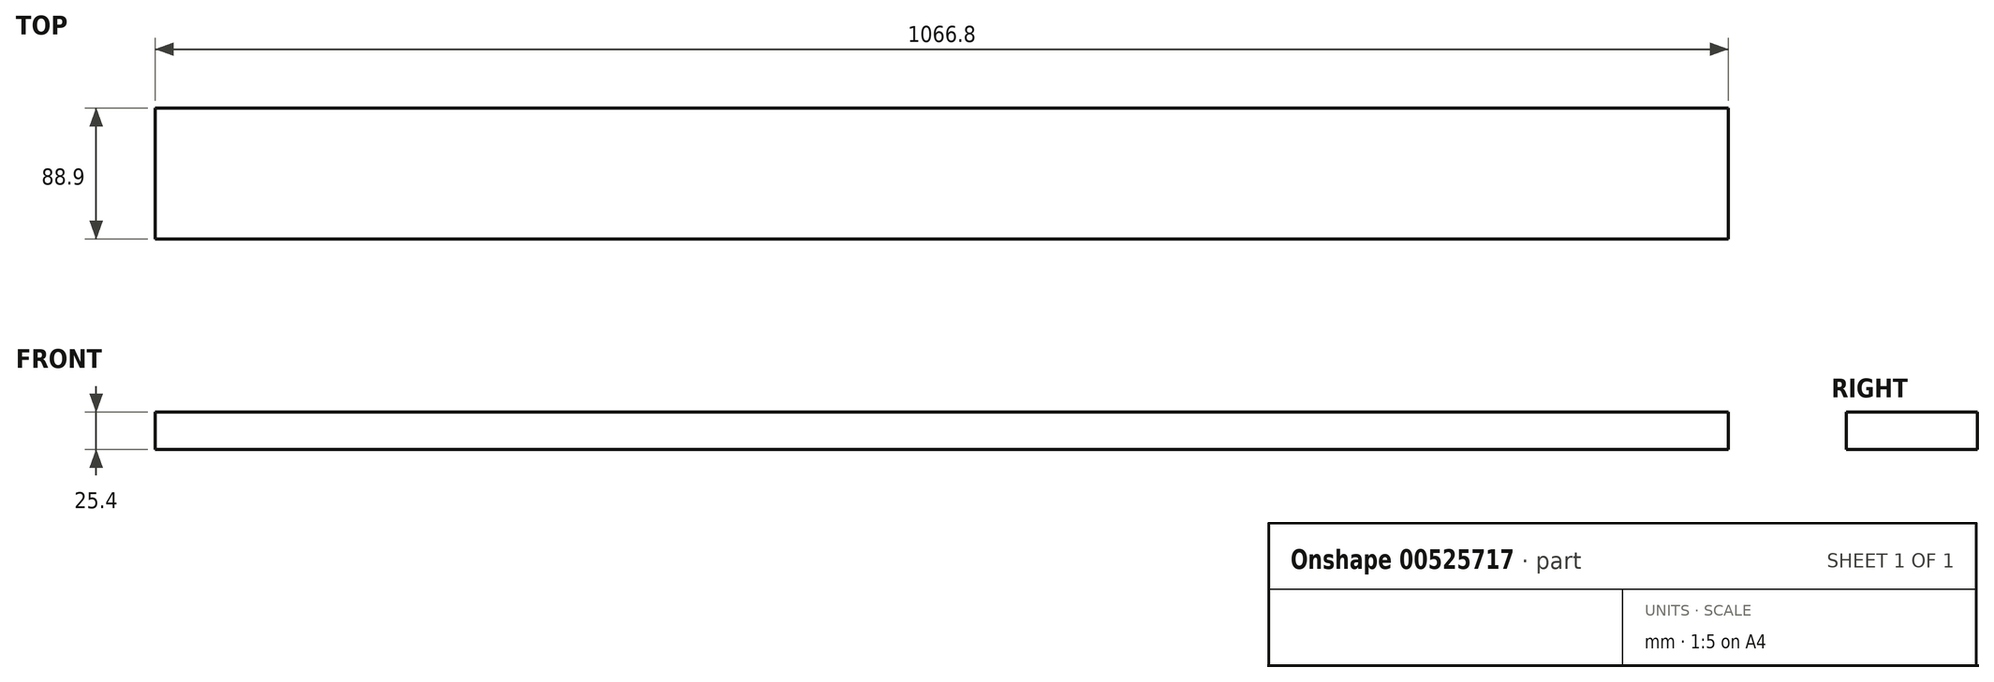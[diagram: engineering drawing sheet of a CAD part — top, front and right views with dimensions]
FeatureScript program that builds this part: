
annotation { "Feature Type Name" : "Feature", "Feature Type Description" : "" }
export const myFeature = defineFeature(function(context is Context, id is Id, definition is map)
    precondition{}
    {
        {
            var Q0;
            Q0=qCreatedBy(makeId("Top.planeOp"),FACE);
            var sketch = newSketch(context, id + "F0", { "sketchPlane" : qUnion([Q0])});
            skLineSegment(sketch, "E0.bottom", {"start": v(-509.87, -41.02) * mm, "end": v(556.93, -41.02) * mm});
            skLineSegment(sketch, "E0.top", {"start": v(-509.87, 47.88) * mm, "end": v(556.93, 47.88) * mm});
            skLineSegment(sketch, "E0.left", {"start": v(-509.87, -41.02) * mm, "end": v(-509.87, 47.88) * mm});
            skLineSegment(sketch, "E0.right", {"start": v(556.93, -41.02) * mm, "end": v(556.93, 47.88) * mm});
            skSolve(sketch);
        }
        {
            var Q0;
            Q0=makeQuery(id+"F0.imprint","IMPRINT",FACE,{"disambiguationData":[TD([[makeQuery(id+"F0.imprint","IMPRINT",EDGE,{"derivedFrom":sQuery(id+"F0.wireOp",EDGE,"E0.bottom")}),1.0]])]});
            extrude(context, id + "F1", {"entities" : qUnion([Q0]), "depth" : 25.4 * mm, "offsetDistance" : 25.4 * mm});
        }
    });
